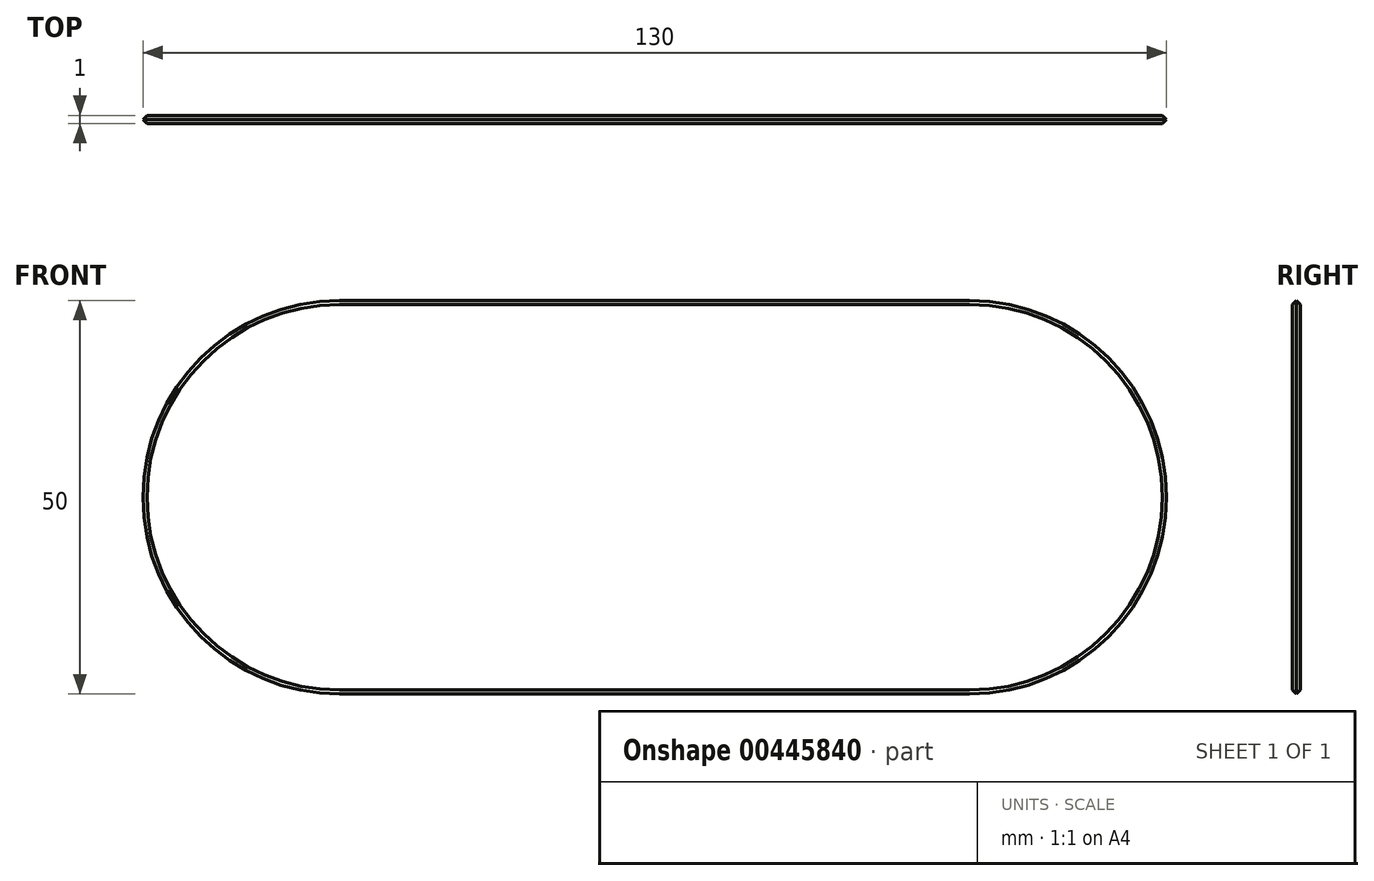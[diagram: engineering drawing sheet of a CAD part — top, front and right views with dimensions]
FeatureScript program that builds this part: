
annotation { "Feature Type Name" : "Feature", "Feature Type Description" : "" }
export const myFeature = defineFeature(function(context is Context, id is Id, definition is map)
    precondition{}
    {
        {
            var Q0;
            Q0=qCreatedBy(makeId("Front.planeOp"),FACE);
            var sketch = newSketch(context, id + "F0", { "sketchPlane" : qUnion([Q0])});
            skLineSegment(sketch, "E0.bottom", {"start": v(40, 25) * mm, "end": v(-40, 25) * mm});
            skLineSegment(sketch, "E0.top", {"start": v(40, -25) * mm, "end": v(-40, -25) * mm});
            skPoint(sketch, "E0.middle", {"position": v(0, 0) * mm});
            skArc(sketch, "E1", {"start": v(40, -25) * mm, "mid": v(65, 0) * mm, "end": v(40, 25) * mm});
            skArc(sketch, "E2", {"start": v(-40, 25) * mm, "mid": v(-65, 0) * mm, "end": v(-40, -25) * mm});
            skSolve(sketch);
        }
        {
            var Q0;
            Q0=makeQuery(id+"F0.imprint","IMPRINT",FACE,{"disambiguationData":[TD([[makeQuery(id+"F0.imprint","IMPRINT",EDGE,{"derivedFrom":sQuery(id+"F0.wireOp",EDGE,"E0.bottom")}),1.0]])]});
            extrude(context, id + "F1", {"entities" : qUnion([Q0]), "depth" : 1 * mm});
        }
        {
            var Q0;
            Q0=makeQuery(id+"F1.opExtrude","CAP_EDGE",EDGE,{"disambiguationData":[OSD([sQuery(id+"F0.wireOp",EDGE,"E0.bottom")])],"isStart":false});
            var Q1;
            Q1=makeQuery(id+"F1.opExtrude","CAP_EDGE",EDGE,{"disambiguationData":[OSD([sQuery(id+"F0.wireOp",EDGE,"E0.bottom")])],"isStart":true});
            chamfer(context, id + "F2", {"entities" : qUnion([Q0, Q1]), "width" : .5 * mm, "tangentPropagation" : true});
        }
    });
